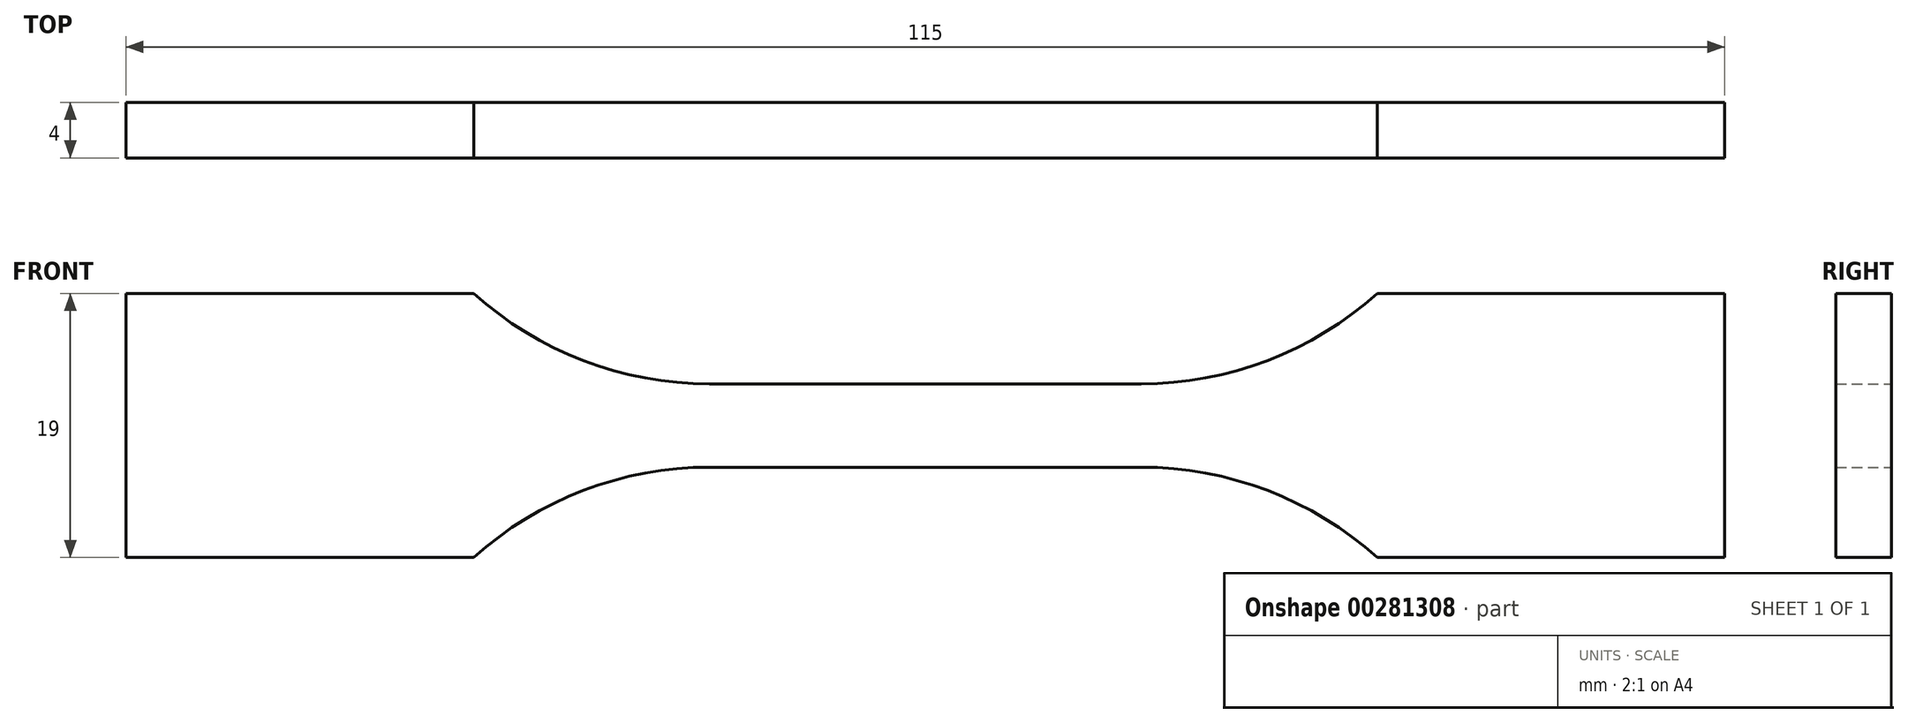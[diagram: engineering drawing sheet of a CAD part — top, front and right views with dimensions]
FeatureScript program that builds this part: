
annotation { "Feature Type Name" : "Feature", "Feature Type Description" : "" }
export const myFeature = defineFeature(function(context is Context, id is Id, definition is map)
    precondition{}
    {
        {
            var Q0;
            Q0=qCreatedBy(makeId("Front.planeOp"),FACE);
            var sketch = newSketch(context, id + "F0", { "sketchPlane" : qUnion([Q0])});
            skLineSegment(sketch, "E0", {"start": v(0, 3) * mm, "end": v(15.53, 3) * mm});
            skArc(sketch, "E1", {"start": v(15.53, 3) * mm, "mid": v(24.62, 4.68) * mm, "end": v(32.5, 9.5) * mm});
            skLineSegment(sketch, "E2", {"start": v(32.5, 9.5) * mm, "end": v(57.5, 9.5) * mm});
            skLineSegment(sketch, "E3", {"start": v(57.5, 9.5) * mm, "end": v(57.5, 0) * mm});
            skLineSegment(sketch, "E4.MirrorCS", {"start": v(0, -3) * mm, "end": v(15.53, -3) * mm});
            skLineSegment(sketch, "E5.MirrorCS", {"start": v(57.5, -9.5) * mm, "end": v(57.5, 0) * mm});
            skLineSegment(sketch, "E6.MirrorCS", {"start": v(32.5, -9.5) * mm, "end": v(57.5, -9.5) * mm});
            skArc(sketch, "E7.MirrorCS", {"start": v(15.53, -3) * mm, "mid": v(24.62, -4.68) * mm, "end": v(32.5, -9.5) * mm});
            skArc(sketch, "E8.MirrorCS", {"start": v(15.53, 3) * mm, "mid": v(22.83, 4.07) * mm, "end": v(29.5, 7.2) * mm});
            skLineSegment(sketch, "E9.MirrorCS", {"start": v(37.2, 9.5) * mm, "end": v(57.5, 9.5) * mm});
            skLineSegment(sketch, "E10.MirrorCS", {"start": v(37.2, -9.5) * mm, "end": v(57.5, -9.5) * mm});
            skArc(sketch, "E11.MirrorCS", {"start": v(15.53, -3) * mm, "mid": v(22.83, -4.07) * mm, "end": v(29.5, -7.2) * mm});
            skLineSegment(sketch, "E12.MirrorCS", {"start": v(0, 3) * mm, "end": v(-15.53, 3) * mm});
            skLineSegment(sketch, "E13.MirrorCS", {"start": v(-57.5, -9.5) * mm, "end": v(-57.5, 0) * mm});
            skArc(sketch, "E14.MirrorCS", {"start": v(-15.53, 3) * mm, "mid": v(-22.83, 4.07) * mm, "end": v(-29.5, 7.2) * mm});
            skLineSegment(sketch, "E15.MirrorCS", {"start": v(-32.5, 9.5) * mm, "end": v(-57.5, 9.5) * mm});
            skLineSegment(sketch, "E16.MirrorCS", {"start": v(-57.5, 9.5) * mm, "end": v(-57.5, 0) * mm});
            skLineSegment(sketch, "E17.MirrorCS", {"start": v(-37.2, -9.5) * mm, "end": v(-57.5, -9.5) * mm});
            skLineSegment(sketch, "E18.MirrorCS", {"start": v(0, -3) * mm, "end": v(-15.53, -3) * mm});
            skArc(sketch, "E19.MirrorCS", {"start": v(-15.53, -3) * mm, "mid": v(-24.62, -4.68) * mm, "end": v(-32.5, -9.5) * mm});
            skArc(sketch, "E20.MirrorCS", {"start": v(-15.53, 3) * mm, "mid": v(-24.62, 4.68) * mm, "end": v(-32.5, 9.5) * mm});
            skLineSegment(sketch, "E21.MirrorCS", {"start": v(-32.5, -9.5) * mm, "end": v(-57.5, -9.5) * mm});
            skArc(sketch, "E22.MirrorCS", {"start": v(-15.53, -3) * mm, "mid": v(-22.83, -4.07) * mm, "end": v(-29.5, -7.2) * mm});
            skLineSegment(sketch, "E23.MirrorCS", {"start": v(-37.2, 9.5) * mm, "end": v(-57.5, 9.5) * mm});
            skPoint(sketch, "E24.visualSharp", {"position": v(32.5, -9.5) * mm});
            skArc(sketch, "E24.filletArc", {"start": v(29.5, -7.2) * mm, "mid": v(33.19, -8.91) * mm, "end": v(37.2, -9.5) * mm});
            skPoint(sketch, "E25.visualSharp", {"position": v(-32.5, 9.5) * mm});
            skArc(sketch, "E25.filletArc", {"start": v(-29.5, 7.2) * mm, "mid": v(-33.19, 8.91) * mm, "end": v(-37.2, 9.5) * mm});
            skPoint(sketch, "E26.visualSharp", {"position": v(-32.5, -9.5) * mm});
            skArc(sketch, "E26.filletArc", {"start": v(-37.2, -9.5) * mm, "mid": v(-33.19, -8.91) * mm, "end": v(-29.5, -7.2) * mm});
            skPoint(sketch, "E27.visualSharp", {"position": v(32.5, 9.5) * mm});
            skArc(sketch, "E27.filletArc", {"start": v(37.2, 9.5) * mm, "mid": v(33.19, 8.91) * mm, "end": v(29.5, 7.2) * mm});
            skSolve(sketch);
        }
        {
            var Q0;
            Q0 = qSketchRegion(id + "F0", true);
            extrude(context, id + "F1", {"entities" : qUnion([Q0]), "endBound" : BoundingType.SYMMETRIC, "depth" : 4 * mm});
        }
    });
